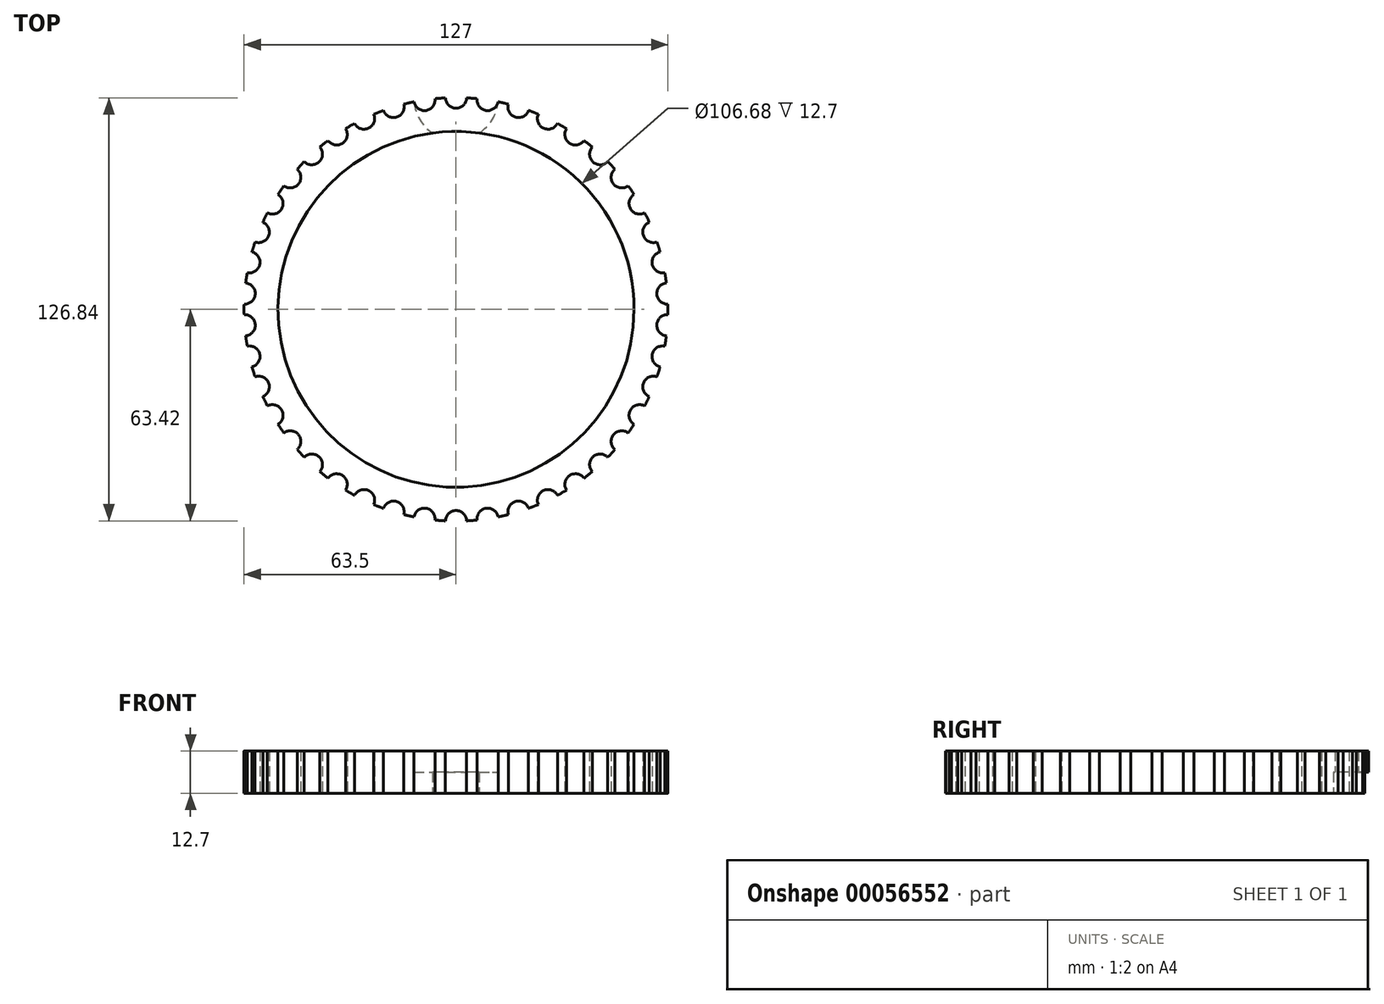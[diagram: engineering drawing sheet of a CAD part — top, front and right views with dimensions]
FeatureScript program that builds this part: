
annotation { "Feature Type Name" : "Feature", "Feature Type Description" : "" }
export const myFeature = defineFeature(function(context is Context, id is Id, definition is map)
    precondition{}
    {
        {
            var Q0;
            Q0=qCreatedBy(makeId("Top.planeOp"),FACE);
            var sketch = newSketch(context, id + "F0", { "sketchPlane" : qUnion([Q0])});
            skCircle(sketch, "E0", {"center": v(0, 0) * mm, "radius": 63.5 * mm});
            skCircle(sketch, "E1", {"center": v(0, 63.5) * mm, "radius": 12.7 * mm});
            skCircle(sketch, "E2", {"center": v(0, 63.5) * mm, "radius": 3.18 * mm});
            skCircle(sketch, "E3", {"center": v(0, 0) * mm, "radius": 53.34 * mm});
            skSolve(sketch);
        }
        {
            var Q0;
            {var subQ0=sQuery(id+"F0.wireOp",EDGE,"E1");var subQ1=sQuery(id+"F0.wireOp",EDGE,"E0");var subQ2=makeQuery(id+"F0.imprint","INTERSECT",VERTEX,{"disambiguationData":[OD(0.0)],"derivedFrom":[subQ1,subQ0]});Q0=makeQuery(id+"F0.imprint","IMPRINT",FACE,{"disambiguationData":[TD([[makeQuery(id+"F0.imprint","IMPRINT",EDGE,{"disambiguationData":[TD([[subQ2,1.0]])],"derivedFrom":subQ1}),1.0]])]});}
            var Q1;
            {var subQ0=sQuery(id+"F0.wireOp",EDGE,"E1");var subQ1=sQuery(id+"F0.wireOp",EDGE,"E0");var subQ2=makeQuery(id+"F0.imprint","INTERSECT",VERTEX,{"disambiguationData":[OD(0.0)],"derivedFrom":[subQ1,subQ0]});Q1=makeQuery(id+"F0.imprint","IMPRINT",FACE,{"disambiguationData":[TD([[makeQuery(id+"F0.imprint","IMPRINT",EDGE,{"disambiguationData":[TD([[subQ2,-1.0]])],"derivedFrom":subQ1}),1.0]])]});}
            var Q2;
            {var subQ0=sQuery(id+"F0.wireOp",EDGE,"E2");var subQ1=sQuery(id+"F0.wireOp",EDGE,"E0");var subQ2=makeQuery(id+"F0.imprint","INTERSECT",VERTEX,{"disambiguationData":[OD(0.0)],"derivedFrom":[subQ1,subQ0]});Q2=makeQuery(id+"F0.imprint","IMPRINT",FACE,{"disambiguationData":[TD([[makeQuery(id+"F0.imprint","IMPRINT",EDGE,{"disambiguationData":[TD([[subQ2,-1.0]])],"derivedFrom":subQ1}),1.0]])]});}
            extrude(context, id + "F1", {"entities" : qUnion([Q0, Q1, Q2]), "depth" : 12.7 * mm});
        }
        {
            var Q0;
            {var subQ0=sQuery(id+"F0.wireOp",EDGE,"E2");var subQ1=sQuery(id+"F0.wireOp",EDGE,"E0");var subQ2=makeQuery(id+"F0.imprint","INTERSECT",VERTEX,{"disambiguationData":[OD(0.0)],"derivedFrom":[subQ1,subQ0]});Q0=makeQuery(id+"F0.imprint","IMPRINT",FACE,{"disambiguationData":[TD([[makeQuery(id+"F0.imprint","IMPRINT",EDGE,{"disambiguationData":[TD([[subQ2,-1.0]])],"derivedFrom":subQ1}),-1.0]])]});}
            var Q1;
            {var subQ0=sQuery(id+"F0.wireOp",EDGE,"E2");var subQ1=sQuery(id+"F0.wireOp",EDGE,"E0");var subQ2=makeQuery(id+"F0.imprint","INTERSECT",VERTEX,{"disambiguationData":[OD(0.0)],"derivedFrom":[subQ1,subQ0]});Q1=makeQuery(id+"F0.imprint","IMPRINT",FACE,{"disambiguationData":[TD([[makeQuery(id+"F0.imprint","IMPRINT",EDGE,{"disambiguationData":[TD([[subQ2,-1.0]])],"derivedFrom":subQ1}),1.0]])]});}
            var Q2;
            Q2=makeQuery(id+"F1.opExtrude","CAP_FACE",FACE,{"disambiguationData":[OSD([sQuery(id+"F0.wireOp",EDGE,"E0"),sQuery(id+"F0.wireOp",EDGE,"E3")])],"isStart":false});
            var Q3;
            Q3=makeQuery(id+"F1.opExtrude","CAP_FACE",FACE,{"disambiguationData":[OSD([sQuery(id+"F0.wireOp",EDGE,"E0"),sQuery(id+"F0.wireOp",EDGE,"E3")])],"isStart":false});
            extrude(context, id + "F2", {"entities" : qUnion([Q0, Q1, Q2]), "operationType" : NewBodyOperationType.REMOVE, "endBound" : BoundingType.THROUGH_ALL, "endBoundEntityFace" : qUnion([Q3]), "depth" : 25.4 * mm});
        }
        {
            var Q0;
            Q0=makeQuery(id+"F2.boolean.opBoolean","COPY",FACE,{"derivedFrom":makeQuery(id+"F2.opExtrude","SWEPT_FACE",FACE,{"disambiguationData":[OSD([sQuery(id+"F0.wireOp",EDGE,"E2")])]})});
            var Q1;
            Q1=makeQuery(id+"F1.opExtrude","SWEPT_FACE",FACE,{"disambiguationData":[OSD([sQuery(id+"F0.wireOp",EDGE,"E3")])]});
            circularPattern(context, id + "F3", {"faces" : qUnion([Q0]), "axis" : qUnion([Q1]), "angle" : 360 * degree, "instanceCount" : 42, "equalSpace" : true, "patternType" : PatternType.FACE});
        }
        {
            var Q0;
            {var subQ0=sQuery(id+"F0.wireOp",EDGE,"E1");var subQ1=sQuery(id+"F0.wireOp",EDGE,"E0");var subQ2=makeQuery(id+"F0.imprint","INTERSECT",VERTEX,{"disambiguationData":[OD(0.0)],"derivedFrom":[subQ1,subQ0]});Q0=makeQuery(id+"F0.imprint","IMPRINT",FACE,{"disambiguationData":[TD([[makeQuery(id+"F0.imprint","IMPRINT",EDGE,{"disambiguationData":[TD([[subQ2,-1.0]])],"derivedFrom":subQ1}),1.0]])]});}
            extrude(context, id + "F4", {"entities" : qUnion([Q0]), "operationType" : NewBodyOperationType.REMOVE, "depth" : 6.35 * mm, "hasSecondDirection" : true, "secondDirectionOppositeDirection" : true, "secondDirectionDepth" : 12.7 * mm});
        }
    });
